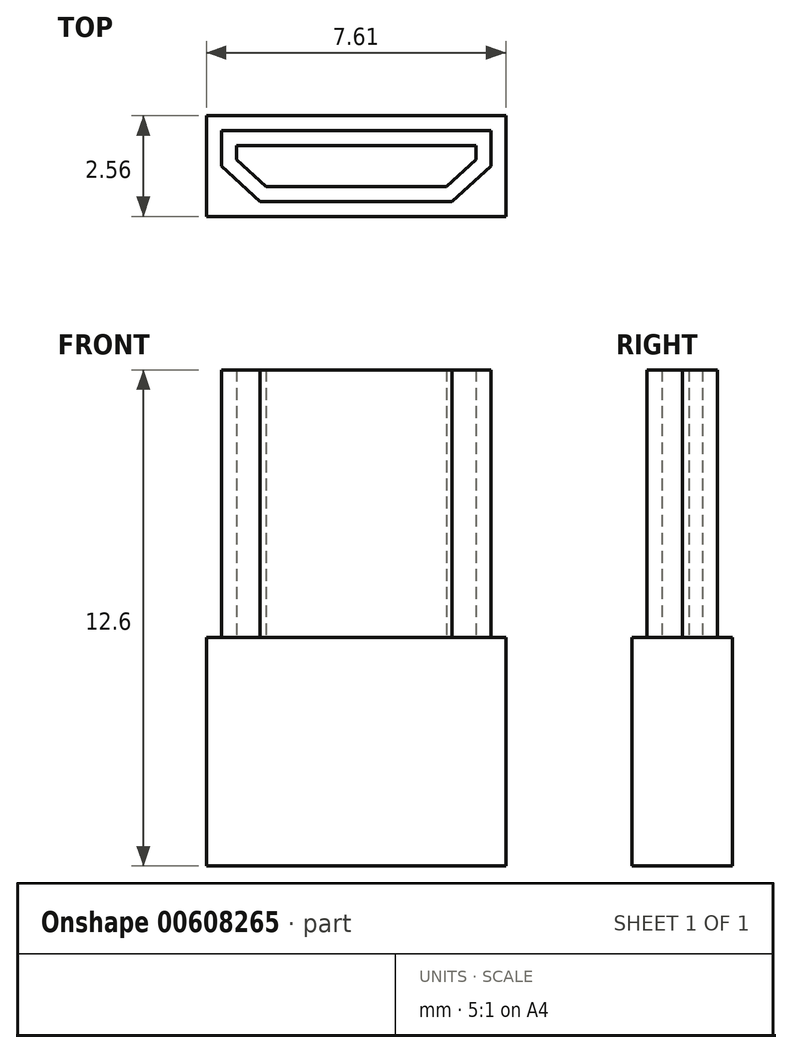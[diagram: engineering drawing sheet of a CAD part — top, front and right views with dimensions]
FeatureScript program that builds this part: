
annotation { "Feature Type Name" : "Feature", "Feature Type Description" : "" }
export const myFeature = defineFeature(function(context is Context, id is Id, definition is map)
    precondition{}
    {
        {
            var Q0;
            Q0=qCreatedBy(makeId("Top.planeOp"),FACE);
            var sketch = newSketch(context, id + "F0", { "sketchPlane" : qUnion([Q0])});
            skLineSegment(sketch, "E0.bottom", {"start": v(0.98, 0) * mm, "end": v(5.87, 0) * mm});
            skLineSegment(sketch, "E0.top", {"start": v(0, 1.8) * mm, "end": v(6.85, 1.8) * mm});
            skLineSegment(sketch, "E0.left", {"start": v(0, 0.9) * mm, "end": v(0, 1.8) * mm});
            skLineSegment(sketch, "E0.right", {"start": v(6.85, 0.9) * mm, "end": v(6.85, 1.8) * mm});
            skLineSegment(sketch, "E1", {"start": v(0, 0.9) * mm, "end": v(0.98, 0) * mm});
            skLineSegment(sketch, "E2.MirrorCS", {"start": v(6.85, 0.9) * mm, "end": v(5.87, 0) * mm});
            skPoint(sketch, "E3.orphan", {"position": v(0, 0) * mm});
            skPoint(sketch, "E4.orphan", {"position": v(6.85, 0) * mm});
            skLineSegment(sketch, "E5.0", {"start": v(0.38, 1.07) * mm, "end": v(0.38, 1.42) * mm});
            skLineSegment(sketch, "E5.1", {"start": v(6.47, 1.07) * mm, "end": v(6.47, 1.42) * mm});
            skLineSegment(sketch, "E5.2", {"start": v(6.47, 1.07) * mm, "end": v(5.72, 0.38) * mm});
            skLineSegment(sketch, "E5.3", {"start": v(0.38, 1.42) * mm, "end": v(6.47, 1.42) * mm});
            skLineSegment(sketch, "E5.4", {"start": v(1.13, 0.38) * mm, "end": v(5.72, 0.38) * mm});
            skLineSegment(sketch, "E5.5", {"start": v(0.38, 1.07) * mm, "end": v(1.13, 0.38) * mm});
            skSolve(sketch);
        }
        {
            var Q0;
            Q0 = qSketchRegion(id + "F0", true);
            extrude(context, id + "F1", {"entities" : qUnion([Q0]), "depth" : 6.8 * mm, "offsetDistance" : 25.4 * mm});
        }
        {
            var Q0;
            Q0=qCreatedBy(makeId("Top.planeOp"),FACE);
            var sketch = newSketch(context, id + "F2", { "sketchPlane" : qUnion([Q0])});
            skLineSegment(sketch, "E6.0", {"start": v(7.23, -0.38) * mm, "end": v(7.23, 2.18) * mm});
            skLineSegment(sketch, "E6.1", {"start": v(-0.38, -0.38) * mm, "end": v(7.23, -0.38) * mm});
            skLineSegment(sketch, "E6.2", {"start": v(-0.38, -0.38) * mm, "end": v(-0.38, 2.18) * mm});
            skLineSegment(sketch, "E6.3", {"start": v(-0.38, 2.18) * mm, "end": v(7.23, 2.18) * mm});
            skSolve(sketch);
        }
        {
            var Q0;
            Q0 = qSketchRegion(id + "F2", true);
            extrude(context, id + "F3", {"entities" : qUnion([Q0]), "operationType" : NewBodyOperationType.ADD, "oppositeDirection" : true, "depth" : 5.8 * mm, "offsetDistance" : 25.4 * mm});
        }
    });
